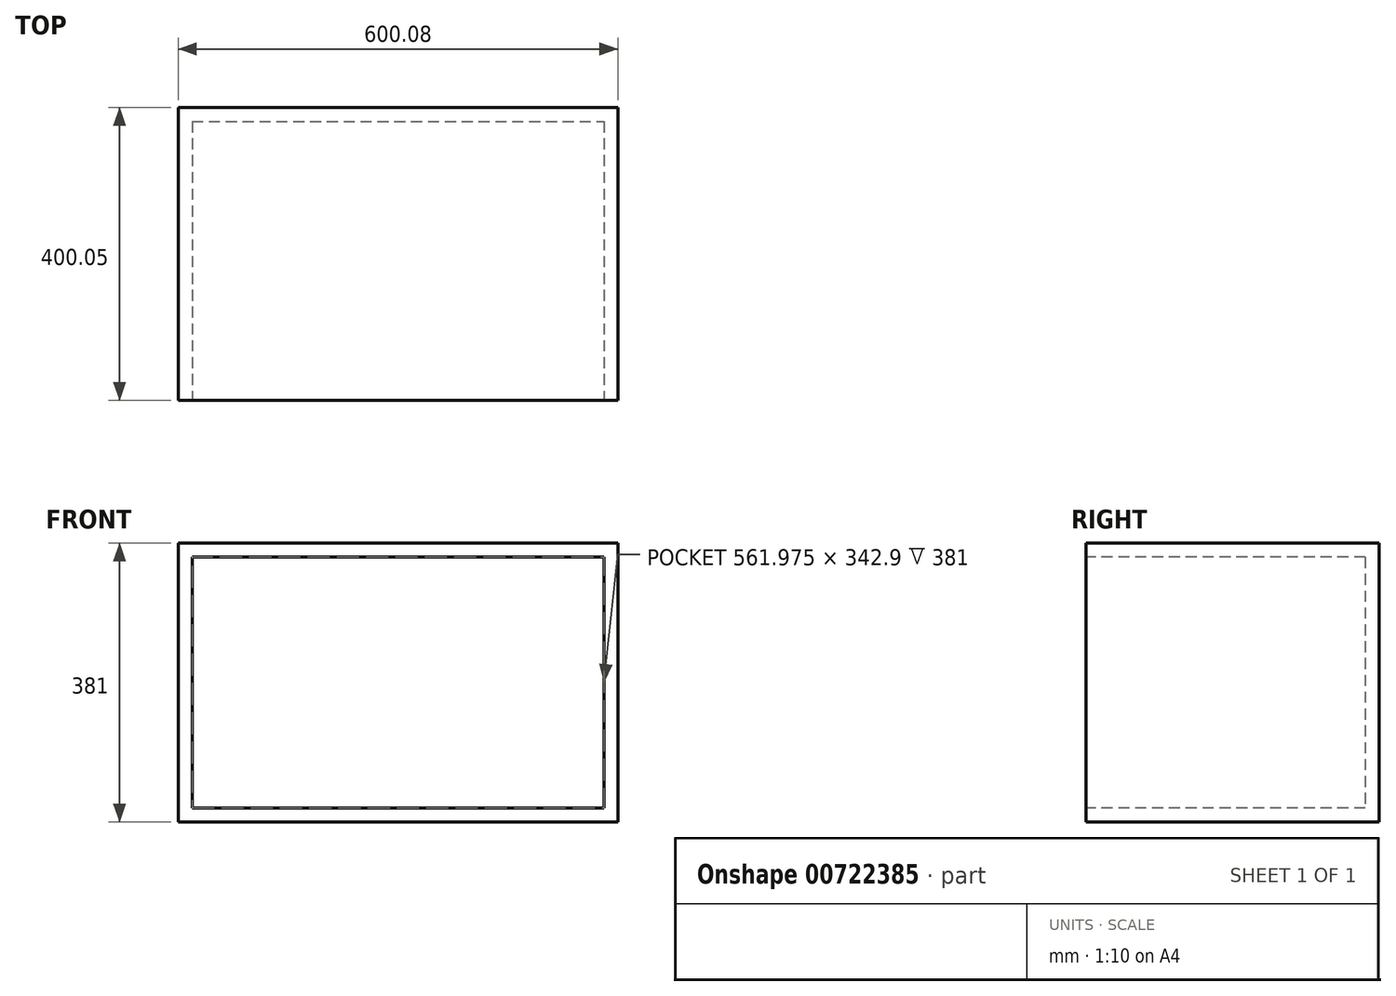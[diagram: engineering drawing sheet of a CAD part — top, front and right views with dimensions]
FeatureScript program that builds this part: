
annotation { "Feature Type Name" : "Feature", "Feature Type Description" : "" }
export const myFeature = defineFeature(function(context is Context, id is Id, definition is map)
    precondition{}
    {
        {
            var Q0;
            Q0=qCreatedBy(makeId("Front.planeOp"),FACE);
            var sketch = newSketch(context, id + "F0", { "sketchPlane" : qUnion([Q0])});
            skLineSegment(sketch, "E0.bottom", {"start": v(0, 0) * mm, "end": v(600.08, 0) * mm});
            skLineSegment(sketch, "E0.top", {"start": v(0, -381) * mm, "end": v(600.08, -381) * mm});
            skLineSegment(sketch, "E0.left", {"start": v(0, 0) * mm, "end": v(0, -381) * mm});
            skLineSegment(sketch, "E0.right", {"start": v(600.08, 0) * mm, "end": v(600.08, -381) * mm});
            skSolve(sketch);
        }
        {
            var Q0;
            Q0=qSketchRegion(id+"F0",true);
            extrude(context, id + "F1", {"entities" : qUnion([Q0]), "oppositeDirection" : true, "depth" : 400.05 * mm, "offsetDistance" : 25.4 * mm});
        }
        {
            var Q0;
            Q0=makeQuery(id+"F1.opExtrude","CAP_FACE",FACE,{"disambiguationData":[OSD([sQuery(id+"F0.wireOp",EDGE,"E0.bottom"),sQuery(id+"F0.wireOp",EDGE,"E0.top"),sQuery(id+"F0.wireOp",EDGE,"E0.left"),sQuery(id+"F0.wireOp",EDGE,"E0.right")])],"isStart":true});
            shell(context, id + "F2", {"entities" : qUnion([Q0]), "thickness" : 19.05 * mm});
        }
    });
